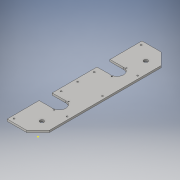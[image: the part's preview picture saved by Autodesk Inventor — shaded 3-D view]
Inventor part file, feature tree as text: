
AUTODESK INVENTOR PART (.ipt)
format: ipt  version: 2016 (Build 200138000, 138)  size: 128,000 bytes
history: native  units: in
note: dims shown in document units (in); Inventor stores cm internally (conversion verified against a paired STEP export)
features: sketch x4, other x2
ambient origin geometry x8: Origin, YZ Plane, XZ Plane, XY Plane, X Axis, Y Axis, Z Axis, Center Point
bodies: Solid1 (feature_tree)
feature tree (6):
  other  "DriveTrainPlate.iam"
  other  "DriveTrainPlate.ipt:1"
  sketch  "Sketch 1"  dims[d0=0.3937in]
  sketch  "Sketch 16"
  sketch  "Sketch 23"
  sketch  "Sketch3"
